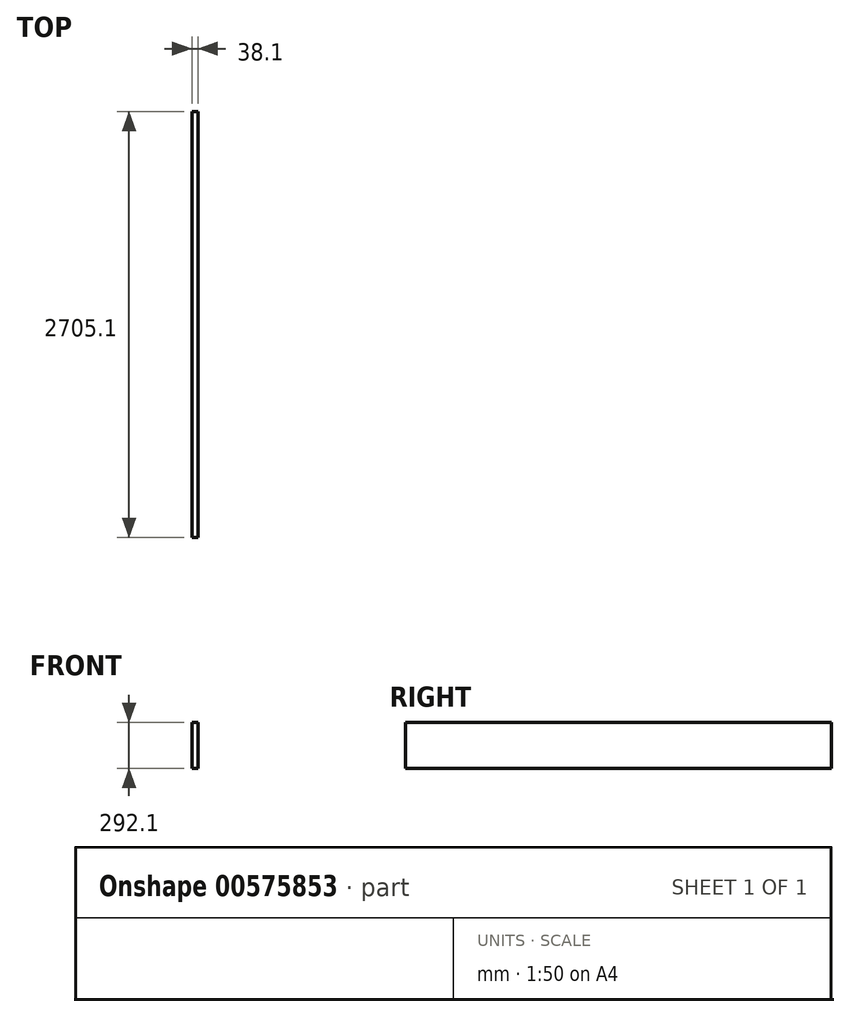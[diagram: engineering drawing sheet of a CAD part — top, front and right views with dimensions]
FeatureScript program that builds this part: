
annotation { "Feature Type Name" : "Feature", "Feature Type Description" : "" }
export const myFeature = defineFeature(function(context is Context, id is Id, definition is map)
    precondition{}
    {
        {
            var Q0;
            Q0=qCreatedBy(makeId("Front.planeOp"),FACE);
            var sketch = newSketch(context, id + "F0", { "sketchPlane" : qUnion([Q0])});
            skLineSegment(sketch, "E0.bottom", {"start": v(0, 0) * mm, "end": v(38.1, 0) * mm});
            skLineSegment(sketch, "E0.top", {"start": v(0, 292.1) * mm, "end": v(38.1, 292.1) * mm});
            skLineSegment(sketch, "E0.left", {"start": v(0, 0) * mm, "end": v(0, 292.1) * mm});
            skLineSegment(sketch, "E0.right", {"start": v(38.1, 0) * mm, "end": v(38.1, 292.1) * mm});
            skSolve(sketch);
        }
        {
            var Q0;
            Q0 = qSketchRegion(id + "F0", true);
            extrude(context, id + "F1", {"entities" : qUnion([Q0]), "depth" : 2705.1 * mm, "offsetDistance" : 25.4 * mm});
        }
    });
